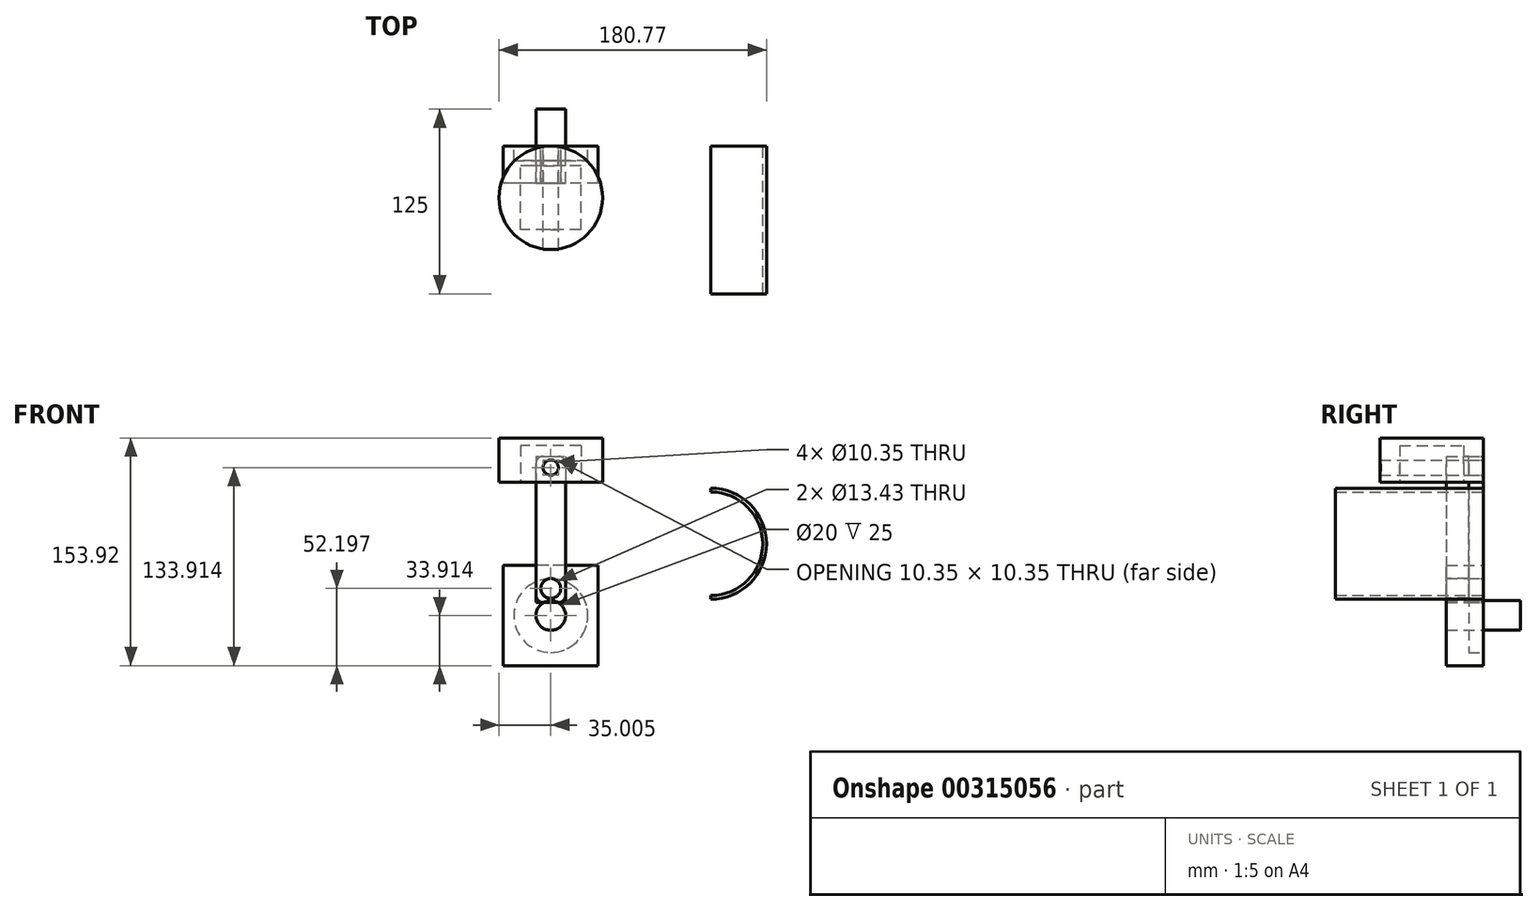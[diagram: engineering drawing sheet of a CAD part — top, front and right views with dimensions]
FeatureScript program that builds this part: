
annotation { "Feature Type Name" : "Feature", "Feature Type Description" : "" }
export const myFeature = defineFeature(function(context is Context, id is Id, definition is map)
    precondition{}
    {
        {
            var Q0;
            Q0=qCreatedBy(makeId("Front.planeOp"),FACE);
            var sketch = newSketch(context, id + "F0", { "sketchPlane" : qUnion([Q0])});
            skCircle(sketch, "E0", {"center": v(-52.9, 10.93) * mm, "radius": 25 * mm});
            skLineSegment(sketch, "E1", {"start": v(-52.9, 19.65) * mm, "end": v(-52.9, 110.93) * mm});
            skLineSegment(sketch, "E2.bottom", {"start": v(-17.9, 100.93) * mm, "end": v(-87.9, 100.93) * mm});
            skLineSegment(sketch, "E2.left", {"start": v(-17.9, 100.93) * mm, "end": v(-17.9, 120.93) * mm});
            skLineSegment(sketch, "E2.right", {"start": v(-87.9, 100.93) * mm, "end": v(-87.9, 120.93) * mm});
            skPoint(sketch, "E2.middle", {"position": v(-52.9, 110.93) * mm});
            skLineSegment(sketch, "E3.left", {"start": v(-62.9, 116.1) * mm, "end": v(-62.9, 19.65) * mm});
            skLineSegment(sketch, "E3.right", {"start": v(-42.9, 116.1) * mm, "end": v(-42.9, 19.65) * mm});
            skPoint(sketch, "E3.middle", {"position": v(-52.9, 60.93) * mm});
            skCircle(sketch, "E4", {"center": v(-52.9, 29.22) * mm, "radius": 6.72 * mm});
            skCircle(sketch, "E5", {"center": v(-52.9, 110.93) * mm, "radius": 5.18 * mm});
            skLineSegment(sketch, "E6.top", {"start": v(-62.9, 118.63) * mm, "end": v(-42.9, 118.63) * mm});
            skLineSegment(sketch, "E6.left", {"start": v(-62.9, 116.1) * mm, "end": v(-62.9, 118.63) * mm});
            skLineSegment(sketch, "E6.right", {"start": v(-42.9, 116.1) * mm, "end": v(-42.9, 118.63) * mm});
            skLineSegment(sketch, "E7.top", {"start": v(-62.9, 19.65) * mm, "end": v(-42.9, 19.65) * mm});
            skPoint(sketch, "E8.orphan", {"position": v(-42.9, 5.76) * mm});
            skPoint(sketch, "E7.bottom.start.orphan", {"position": v(-62.9, 5.76) * mm});
            skLineSegment(sketch, "E9.top", {"start": v(-17.9, 130.94) * mm, "end": v(-87.9, 130.94) * mm});
            skLineSegment(sketch, "E9.left", {"start": v(-17.9, 120.93) * mm, "end": v(-17.9, 130.94) * mm});
            skLineSegment(sketch, "E9.right", {"start": v(-87.9, 120.93) * mm, "end": v(-87.9, 130.94) * mm});
            skCircle(sketch, "E10", {"center": v(-52.9, 10.93) * mm, "radius": 10 * mm});
            skLineSegment(sketch, "E11.bottom", {"start": v(-20.83, 44.84) * mm, "end": v(-84.98, 44.84) * mm});
            skLineSegment(sketch, "E11.top", {"start": v(-20.83, -22.98) * mm, "end": v(-84.98, -22.98) * mm});
            skLineSegment(sketch, "E11.left", {"start": v(-20.83, 44.84) * mm, "end": v(-20.83, -22.98) * mm});
            skLineSegment(sketch, "E11.right", {"start": v(-84.98, 44.84) * mm, "end": v(-84.98, -22.98) * mm});
            skSolve(sketch);
        }
        {
            var Q0;
            Q0=makeQuery(id+"F0.imprint","IMPRINT",FACE,{"disambiguationData":[TD([[makeQuery(id+"F0.imprint","IMPRINT",EDGE,{"derivedFrom":sQuery(id+"F0.wireOp",EDGE,"E2.top")}),1.0]])]});
            var Q1;
            Q1=makeQuery(id+"F0.imprint","IMPRINT",FACE,{"disambiguationData":[TD([[makeQuery(id+"F0.imprint","IMPRINT",EDGE,{"derivedFrom":sQuery(id+"F0.wireOp",EDGE,"E5")}),-1.0]])]});
            var Q2;
            {var subQ7=sQuery(id+"F0.wireOp",EDGE,"E2.left");Q2=makeQuery(id+"F0.imprint","IMPRINT",FACE,{"disambiguationData":[TD([[makeQuery(id+"F0.imprint","IMPRINT",EDGE,{"derivedFrom":subQ7}),1.0]])]});}
            extrude(context, id + "F1", {"entities" : qUnion([Q0, Q1, Q2]), "depth" : 70 * mm});
        }
        {
            var Q0;
            Q0=makeQuery(id+"F1.opExtrude","SWEPT_FACE",FACE,{"disambiguationData":[OSD([sQuery(id+"F0.wireOp",EDGE,"E9.top")])]});
            var sketch = newSketch(context, id + "F2", { "sketchPlane" : qUnion([Q0])});
            skLineSegment(sketch, "E12", {"start": v(-52.9, 0) * mm, "end": v(-52.9, -70) * mm});
            skLineSegment(sketch, "E13", {"start": v(-87.9, -35) * mm, "end": v(-17.9, -35) * mm});
            skCircle(sketch, "E14", {"center": v(-52.9, -35) * mm, "radius": 35 * mm});
            skSolve(sketch);
        }
        {
            var Q0;
            {var subQ1=sQuery(id+"F0.wireOp",EDGE,"E9.top");var subQ2=makeQuery(id+"F1.opExtrude","CAP_EDGE",EDGE,{"disambiguationData":[OSD([subQ1])],"isStart":true});var subQ4=makeQuery(id+"F1.opExtrude","SWEPT_EDGE",EDGE,{"disambiguationData":[OSD([subQ1,sQuery(id+"F0.wireOp",EDGE,"E9.left")])]});var subQ6=makeQuery(id+"F2.imprint","INTERSECT",VERTEX,{"derivedFrom":[subQ4,subQ2]});Q0=makeQuery(id+"F2.imprint","IMPRINT",FACE,{"disambiguationData":[TD([[makeQuery(id+"F2.imprint","IMPRINT",EDGE,{"disambiguationData":[TD([[subQ6,-1.0]])],"derivedFrom":subQ2}),1.0]])]});}
            var Q1;
            {var subQ1=sQuery(id+"F0.wireOp",EDGE,"E9.top");var subQ2=makeQuery(id+"F1.opExtrude","CAP_EDGE",EDGE,{"disambiguationData":[OSD([subQ1])],"isStart":false});var subQ4=makeQuery(id+"F1.opExtrude","SWEPT_EDGE",EDGE,{"disambiguationData":[OSD([subQ1,sQuery(id+"F0.wireOp",EDGE,"E9.right")])]});var subQ6=makeQuery(id+"F2.imprint","INTERSECT",VERTEX,{"derivedFrom":[subQ4,subQ2]});Q1=makeQuery(id+"F2.imprint","IMPRINT",FACE,{"disambiguationData":[TD([[makeQuery(id+"F2.imprint","IMPRINT",EDGE,{"disambiguationData":[TD([[subQ6,1.0]])],"derivedFrom":subQ2}),-1.0]])]});}
            var Q2;
            {var subQ1=sQuery(id+"F0.wireOp",EDGE,"E9.top");var subQ2=makeQuery(id+"F1.opExtrude","CAP_EDGE",EDGE,{"disambiguationData":[OSD([subQ1])],"isStart":false});var subQ4=makeQuery(id+"F1.opExtrude","SWEPT_EDGE",EDGE,{"disambiguationData":[OSD([subQ1,sQuery(id+"F0.wireOp",EDGE,"E9.left")])]});var subQ6=makeQuery(id+"F2.imprint","INTERSECT",VERTEX,{"derivedFrom":[subQ4,subQ2]});Q2=makeQuery(id+"F2.imprint","IMPRINT",FACE,{"disambiguationData":[TD([[makeQuery(id+"F2.imprint","IMPRINT",EDGE,{"disambiguationData":[TD([[subQ6,-1.0]])],"derivedFrom":subQ2}),-1.0]])]});}
            var Q3;
            {var subQ1=sQuery(id+"F0.wireOp",EDGE,"E9.top");var subQ2=makeQuery(id+"F1.opExtrude","CAP_EDGE",EDGE,{"disambiguationData":[OSD([subQ1])],"isStart":true});var subQ4=makeQuery(id+"F1.opExtrude","SWEPT_EDGE",EDGE,{"disambiguationData":[OSD([subQ1,sQuery(id+"F0.wireOp",EDGE,"E9.right")])]});var subQ6=makeQuery(id+"F2.imprint","INTERSECT",VERTEX,{"derivedFrom":[subQ4,subQ2]});Q3=makeQuery(id+"F2.imprint","IMPRINT",FACE,{"disambiguationData":[TD([[makeQuery(id+"F2.imprint","IMPRINT",EDGE,{"disambiguationData":[TD([[subQ6,1.0]])],"derivedFrom":subQ2}),1.0]])]});}
            extrude(context, id + "F3", {"entities" : qUnion([Q0, Q1, Q2, Q3]), "operationType" : NewBodyOperationType.REMOVE, "oppositeDirection" : true, "depth" : 39.5 * mm});
        }
        {
            var Q0;
            Q0=makeQuery(id+"F1.opExtrude","SWEPT_FACE",FACE,{"disambiguationData":[OSD([sQuery(id+"F0.wireOp",EDGE,"E2.bottom")])]});
            var sketch = newSketch(context, id + "F4", { "sketchPlane" : qUnion([Q0])});
            skLineSegment(sketch, "E15", {"start": v(-52.9, 0) * mm, "end": v(-52.9, 70) * mm});
            skLineSegment(sketch, "E16.bottom", {"start": v(-32.5, 56.64) * mm, "end": v(-73.31, 56.64) * mm});
            skLineSegment(sketch, "E16.top", {"start": v(-32.5, 13.36) * mm, "end": v(-73.31, 13.36) * mm});
            skLineSegment(sketch, "E16.left", {"start": v(-32.5, 56.64) * mm, "end": v(-32.5, 13.36) * mm});
            skLineSegment(sketch, "E16.right", {"start": v(-73.31, 56.64) * mm, "end": v(-73.31, 13.36) * mm});
            skPoint(sketch, "E16.middle", {"position": v(-52.9, 35) * mm});
            skSolve(sketch);
        }
        {
            var Q0;
            {var subQ5=sQuery(id+"F4.wireOp",EDGE,"E16.left");Q0=makeQuery(id+"F4.imprint","IMPRINT",FACE,{"disambiguationData":[TD([[makeQuery(id+"F4.imprint","IMPRINT",EDGE,{"derivedFrom":subQ5}),-1.0]])]});}
            var Q1;
            {var subQ5=sQuery(id+"F4.wireOp",EDGE,"E16.right");Q1=makeQuery(id+"F4.imprint","IMPRINT",FACE,{"disambiguationData":[TD([[makeQuery(id+"F4.imprint","IMPRINT",EDGE,{"derivedFrom":subQ5}),1.0]])]});}
            extrude(context, id + "F5", {"entities" : qUnion([Q0, Q1]), "operationType" : NewBodyOperationType.REMOVE, "oppositeDirection" : true, "depth" : 25 * mm});
        }
        {
            var Q0;
            Q0=makeQuery(id+"F0.imprint","IMPRINT",FACE,{"disambiguationData":[TD([[makeQuery(id+"F0.imprint","IMPRINT",EDGE,{"derivedFrom":sQuery(id+"F0.wireOp",EDGE,"E5")}),1.0]])]});
            extrude(context, id + "F6", {"entities" : qUnion([Q0]), "depth" : 70 * mm});
        }
        {
            var Q0;
            {var subQ5=sQuery(id+"F0.wireOp",EDGE,"E0");var subQ7=sQuery(id+"F0.wireOp",EDGE,"E3.right");var subQ9=makeQuery(id+"F0.imprint","INTERSECT",VERTEX,{"derivedFrom":[subQ5,subQ7]});Q0=makeQuery(id+"F0.imprint","IMPRINT",FACE,{"disambiguationData":[TD([[makeQuery(id+"F0.imprint","IMPRINT",EDGE,{"disambiguationData":[TD([[subQ9,1.0]])],"derivedFrom":subQ5}),1.0]])]});}
            var Q1;
            {var subQ0=sQuery(id+"F0.wireOp",EDGE,"E7.top");var subQ1=makeQuery(id+"F0.imprint","INTERSECT",VERTEX,{"derivedFrom":[sQuery(id+"F0.wireOp",EDGE,"E1"),subQ0]});Q1=makeQuery(id+"F0.imprint","IMPRINT",FACE,{"disambiguationData":[TD([[makeQuery(id+"F0.imprint","IMPRINT",EDGE,{"disambiguationData":[TD([[subQ1,1.0]])],"derivedFrom":subQ0}),-1.0]])]});}
            var Q2;
            {var subQ1=sQuery(id+"F0.wireOp",EDGE,"E1");var subQ9=sQuery(id+"F0.wireOp",EDGE,"E10");var subQ11=makeQuery(id+"F0.imprint","INTERSECT",VERTEX,{"derivedFrom":[subQ1,subQ9]});Q2=makeQuery(id+"F0.imprint","IMPRINT",FACE,{"disambiguationData":[TD([[makeQuery(id+"F0.imprint","IMPRINT",EDGE,{"disambiguationData":[TD([[subQ11,-1.0]])],"derivedFrom":subQ1}),1.0]])]});}
            var Q3;
            {var subQ0=sQuery(id+"F0.wireOp",EDGE,"E4");var subQ1=sQuery(id+"F0.wireOp",EDGE,"E1");var subQ2=makeQuery(id+"F0.imprint","INTERSECT",VERTEX,{"derivedFrom":[subQ1,subQ0]});Q3=makeQuery(id+"F0.imprint","IMPRINT",FACE,{"disambiguationData":[TD([[makeQuery(id+"F0.imprint","IMPRINT",EDGE,{"disambiguationData":[TD([[subQ2,-1.0]])],"derivedFrom":subQ1}),1.0]])]});}
            var Q4;
            {var subQ0=sQuery(id+"F0.wireOp",EDGE,"E4");var subQ1=sQuery(id+"F0.wireOp",EDGE,"E1");var subQ2=makeQuery(id+"F0.imprint","INTERSECT",VERTEX,{"derivedFrom":[subQ1,subQ0]});Q4=makeQuery(id+"F0.imprint","IMPRINT",FACE,{"disambiguationData":[TD([[makeQuery(id+"F0.imprint","IMPRINT",EDGE,{"disambiguationData":[TD([[subQ2,-1.0]])],"derivedFrom":subQ1}),-1.0]])]});}
            var Q5;
            {var subQ0=sQuery(id+"F0.wireOp",EDGE,"E7.top");var subQ1=sQuery(id+"F0.wireOp",EDGE,"E1");var subQ2=makeQuery(id+"F0.imprint","INTERSECT",VERTEX,{"derivedFrom":[subQ1,subQ0]});Q5=makeQuery(id+"F0.imprint","IMPRINT",FACE,{"disambiguationData":[TD([[makeQuery(id+"F0.imprint","IMPRINT",EDGE,{"disambiguationData":[TD([[subQ2,-1.0]])],"derivedFrom":subQ1}),-1.0]])]});}
            var Q6;
            {var subQ0=sQuery(id+"F0.wireOp",EDGE,"E7.top");var subQ1=sQuery(id+"F0.wireOp",EDGE,"E1");var subQ2=makeQuery(id+"F0.imprint","INTERSECT",VERTEX,{"derivedFrom":[subQ1,subQ0]});Q6=makeQuery(id+"F0.imprint","IMPRINT",FACE,{"disambiguationData":[TD([[makeQuery(id+"F0.imprint","IMPRINT",EDGE,{"disambiguationData":[TD([[subQ2,-1.0]])],"derivedFrom":subQ1}),1.0]])]});}
            var Q7;
            {var subQ1=sQuery(id+"F0.wireOp",EDGE,"E1");var subQ9=sQuery(id+"F0.wireOp",EDGE,"E10");var subQ10=makeQuery(id+"F0.imprint","INTERSECT",VERTEX,{"derivedFrom":[subQ1,subQ9]});Q7=makeQuery(id+"F0.imprint","IMPRINT",FACE,{"disambiguationData":[TD([[makeQuery(id+"F0.imprint","IMPRINT",EDGE,{"disambiguationData":[TD([[subQ10,-1.0]])],"derivedFrom":subQ1}),-1.0]])]});}
            extrude(context, id + "F7", {"entities" : qUnion([Q0, Q1, Q2, Q3, Q4, Q5, Q6, Q7]), "depth" : 10 * mm});
        }
        {
            var Q0;
            {var subQ0=sQuery(id+"F0.wireOp",EDGE,"E4");var subQ1=sQuery(id+"F0.wireOp",EDGE,"E1");var subQ2=makeQuery(id+"F0.imprint","INTERSECT",VERTEX,{"derivedFrom":[subQ1,subQ0]});Q0=makeQuery(id+"F0.imprint","IMPRINT",FACE,{"disambiguationData":[TD([[makeQuery(id+"F0.imprint","IMPRINT",EDGE,{"disambiguationData":[TD([[subQ2,-1.0]])],"derivedFrom":subQ1}),-1.0]])]});}
            var Q1;
            {var subQ0=sQuery(id+"F0.wireOp",EDGE,"E4");var subQ1=sQuery(id+"F0.wireOp",EDGE,"E1");var subQ2=makeQuery(id+"F0.imprint","INTERSECT",VERTEX,{"derivedFrom":[subQ1,subQ0]});Q1=makeQuery(id+"F0.imprint","IMPRINT",FACE,{"disambiguationData":[TD([[makeQuery(id+"F0.imprint","IMPRINT",EDGE,{"disambiguationData":[TD([[subQ2,-1.0]])],"derivedFrom":subQ1}),1.0]])]});}
            extrude(context, id + "F8", {"entities" : qUnion([Q0, Q1]), "operationType" : NewBodyOperationType.ADD, "depth" : 25 * mm});
        }
        {
            var Q0;
            {var subQ0=sQuery(id+"F0.wireOp",EDGE,"E7.top");var subQ1=makeQuery(id+"F0.imprint","INTERSECT",VERTEX,{"derivedFrom":[sQuery(id+"F0.wireOp",EDGE,"E1"),subQ0]});Q0=makeQuery(id+"F0.imprint","IMPRINT",FACE,{"disambiguationData":[TD([[makeQuery(id+"F0.imprint","IMPRINT",EDGE,{"disambiguationData":[TD([[subQ1,1.0]])],"derivedFrom":subQ0}),-1.0]])]});}
            var Q1;
            {var subQ0=sQuery(id+"F0.wireOp",EDGE,"E7.top");var subQ1=sQuery(id+"F0.wireOp",EDGE,"E1");var subQ2=makeQuery(id+"F0.imprint","INTERSECT",VERTEX,{"derivedFrom":[subQ1,subQ0]});Q1=makeQuery(id+"F0.imprint","IMPRINT",FACE,{"disambiguationData":[TD([[makeQuery(id+"F0.imprint","IMPRINT",EDGE,{"disambiguationData":[TD([[subQ2,-1.0]])],"derivedFrom":subQ1}),1.0]])]});}
            var Q2;
            {var subQ0=sQuery(id+"F0.wireOp",EDGE,"E7.top");var subQ1=sQuery(id+"F0.wireOp",EDGE,"E1");var subQ2=makeQuery(id+"F0.imprint","INTERSECT",VERTEX,{"derivedFrom":[subQ1,subQ0]});Q2=makeQuery(id+"F0.imprint","IMPRINT",FACE,{"disambiguationData":[TD([[makeQuery(id+"F0.imprint","IMPRINT",EDGE,{"disambiguationData":[TD([[subQ2,-1.0]])],"derivedFrom":subQ1}),-1.0]])]});}
            extrude(context, id + "F9", {"entities" : qUnion([Q0, Q1, Q2]), "operationType" : NewBodyOperationType.ADD, "oppositeDirection" : true, "depth" : 25 * mm});
        }
        {
            var Q0;
            Q0=makeQuery(id+"F0.imprint","IMPRINT",FACE,{"disambiguationData":[TD([[makeQuery(id+"F0.imprint","IMPRINT",EDGE,{"derivedFrom":sQuery(id+"F0.wireOp",EDGE,"E11.top")}),-1.0]])]});
            var Q1;
            {var subQ0=sQuery(id+"F0.wireOp",EDGE,"E3.right");var subQ5=sQuery(id+"F0.wireOp",EDGE,"E11.bottom");var subQ6=makeQuery(id+"F0.imprint","INTERSECT",VERTEX,{"derivedFrom":[subQ0,subQ5]});Q1=makeQuery(id+"F0.imprint","IMPRINT",FACE,{"disambiguationData":[TD([[makeQuery(id+"F0.imprint","IMPRINT",EDGE,{"disambiguationData":[TD([[subQ6,-1.0]])],"derivedFrom":subQ0}),-1.0]])]});}
            var Q2;
            {var subQ0=sQuery(id+"F0.wireOp",EDGE,"E3.left");var subQ5=sQuery(id+"F0.wireOp",EDGE,"E11.bottom");var subQ7=makeQuery(id+"F0.imprint","INTERSECT",VERTEX,{"derivedFrom":[subQ0,subQ5]});Q2=makeQuery(id+"F0.imprint","IMPRINT",FACE,{"disambiguationData":[TD([[makeQuery(id+"F0.imprint","IMPRINT",EDGE,{"disambiguationData":[TD([[subQ7,-1.0]])],"derivedFrom":subQ0}),1.0]])]});}
            var Q3;
            {var subQ5=sQuery(id+"F0.wireOp",EDGE,"E0");var subQ7=sQuery(id+"F0.wireOp",EDGE,"E3.right");var subQ9=makeQuery(id+"F0.imprint","INTERSECT",VERTEX,{"derivedFrom":[subQ5,subQ7]});Q3=makeQuery(id+"F0.imprint","IMPRINT",FACE,{"disambiguationData":[TD([[makeQuery(id+"F0.imprint","IMPRINT",EDGE,{"disambiguationData":[TD([[subQ9,1.0]])],"derivedFrom":subQ5}),1.0]])]});}
            var Q4;
            {var subQ1=sQuery(id+"F0.wireOp",EDGE,"E1");var subQ9=sQuery(id+"F0.wireOp",EDGE,"E10");var subQ11=makeQuery(id+"F0.imprint","INTERSECT",VERTEX,{"derivedFrom":[subQ1,subQ9]});Q4=makeQuery(id+"F0.imprint","IMPRINT",FACE,{"disambiguationData":[TD([[makeQuery(id+"F0.imprint","IMPRINT",EDGE,{"disambiguationData":[TD([[subQ11,-1.0]])],"derivedFrom":subQ1}),1.0]])]});}
            var Q5;
            {var subQ1=sQuery(id+"F0.wireOp",EDGE,"E1");var subQ9=sQuery(id+"F0.wireOp",EDGE,"E10");var subQ10=makeQuery(id+"F0.imprint","INTERSECT",VERTEX,{"derivedFrom":[subQ1,subQ9]});Q5=makeQuery(id+"F0.imprint","IMPRINT",FACE,{"disambiguationData":[TD([[makeQuery(id+"F0.imprint","IMPRINT",EDGE,{"disambiguationData":[TD([[subQ10,-1.0]])],"derivedFrom":subQ1}),-1.0]])]});}
            var Q6;
            {var subQ0=sQuery(id+"F0.wireOp",EDGE,"E4");var subQ1=sQuery(id+"F0.wireOp",EDGE,"E1");var subQ2=makeQuery(id+"F0.imprint","INTERSECT",VERTEX,{"derivedFrom":[subQ1,subQ0]});Q6=makeQuery(id+"F0.imprint","IMPRINT",FACE,{"disambiguationData":[TD([[makeQuery(id+"F0.imprint","IMPRINT",EDGE,{"disambiguationData":[TD([[subQ2,-1.0]])],"derivedFrom":subQ1}),-1.0]])]});}
            var Q7;
            {var subQ0=sQuery(id+"F0.wireOp",EDGE,"E4");var subQ1=sQuery(id+"F0.wireOp",EDGE,"E1");var subQ2=makeQuery(id+"F0.imprint","INTERSECT",VERTEX,{"derivedFrom":[subQ1,subQ0]});Q7=makeQuery(id+"F0.imprint","IMPRINT",FACE,{"disambiguationData":[TD([[makeQuery(id+"F0.imprint","IMPRINT",EDGE,{"disambiguationData":[TD([[subQ2,-1.0]])],"derivedFrom":subQ1}),1.0]])]});}
            extrude(context, id + "F10", {"entities" : qUnion([Q0, Q1, Q2, Q3, Q4, Q5, Q6, Q7]), "depth" : 25 * mm});
        }
        {
            var Q0;
            Q0=makeQuery(id+"F0.imprint","IMPRINT",FACE,{"disambiguationData":[TD([[makeQuery(id+"F0.imprint","IMPRINT",EDGE,{"derivedFrom":sQuery(id+"F0.wireOp",EDGE,"E5")}),-1.0]])]});
            var Q1;
            {var subQ0=sQuery(id+"F0.wireOp",EDGE,"E2.bottom");var subQ1=sQuery(id+"F0.wireOp",EDGE,"E1");var subQ2=makeQuery(id+"F0.imprint","INTERSECT",VERTEX,{"derivedFrom":[subQ1,subQ0]});Q1=makeQuery(id+"F0.imprint","IMPRINT",FACE,{"disambiguationData":[TD([[makeQuery(id+"F0.imprint","IMPRINT",EDGE,{"disambiguationData":[TD([[subQ2,1.0]])],"derivedFrom":subQ1}),1.0]])]});}
            var Q2;
            {var subQ0=sQuery(id+"F0.wireOp",EDGE,"E2.bottom");var subQ1=sQuery(id+"F0.wireOp",EDGE,"E1");var subQ2=makeQuery(id+"F0.imprint","INTERSECT",VERTEX,{"derivedFrom":[subQ1,subQ0]});Q2=makeQuery(id+"F0.imprint","IMPRINT",FACE,{"disambiguationData":[TD([[makeQuery(id+"F0.imprint","IMPRINT",EDGE,{"disambiguationData":[TD([[subQ2,1.0]])],"derivedFrom":subQ1}),-1.0]])]});}
            var Q3;
            {var subQ0=sQuery(id+"F0.wireOp",EDGE,"E3.left");var subQ5=sQuery(id+"F0.wireOp",EDGE,"E11.bottom");var subQ7=makeQuery(id+"F0.imprint","INTERSECT",VERTEX,{"derivedFrom":[subQ0,subQ5]});Q3=makeQuery(id+"F0.imprint","IMPRINT",FACE,{"disambiguationData":[TD([[makeQuery(id+"F0.imprint","IMPRINT",EDGE,{"disambiguationData":[TD([[subQ7,-1.0]])],"derivedFrom":subQ0}),1.0]])]});}
            var Q4;
            {var subQ0=sQuery(id+"F0.wireOp",EDGE,"E3.right");var subQ5=sQuery(id+"F0.wireOp",EDGE,"E11.bottom");var subQ6=makeQuery(id+"F0.imprint","INTERSECT",VERTEX,{"derivedFrom":[subQ0,subQ5]});Q4=makeQuery(id+"F0.imprint","IMPRINT",FACE,{"disambiguationData":[TD([[makeQuery(id+"F0.imprint","IMPRINT",EDGE,{"disambiguationData":[TD([[subQ6,-1.0]])],"derivedFrom":subQ0}),-1.0]])]});}
            var Q5;
            {var subQ1=sQuery(id+"F0.wireOp",EDGE,"E1");var subQ9=sQuery(id+"F0.wireOp",EDGE,"E10");var subQ11=makeQuery(id+"F0.imprint","INTERSECT",VERTEX,{"derivedFrom":[subQ1,subQ9]});Q5=makeQuery(id+"F0.imprint","IMPRINT",FACE,{"disambiguationData":[TD([[makeQuery(id+"F0.imprint","IMPRINT",EDGE,{"disambiguationData":[TD([[subQ11,-1.0]])],"derivedFrom":subQ1}),1.0]])]});}
            var Q6;
            {var subQ1=sQuery(id+"F0.wireOp",EDGE,"E1");var subQ9=sQuery(id+"F0.wireOp",EDGE,"E10");var subQ10=makeQuery(id+"F0.imprint","INTERSECT",VERTEX,{"derivedFrom":[subQ1,subQ9]});Q6=makeQuery(id+"F0.imprint","IMPRINT",FACE,{"disambiguationData":[TD([[makeQuery(id+"F0.imprint","IMPRINT",EDGE,{"disambiguationData":[TD([[subQ10,-1.0]])],"derivedFrom":subQ1}),-1.0]])]});}
            var Q7;
            {var subQ0=sQuery(id+"F0.wireOp",EDGE,"E7.top");var subQ1=sQuery(id+"F0.wireOp",EDGE,"E1");var subQ2=makeQuery(id+"F0.imprint","INTERSECT",VERTEX,{"derivedFrom":[subQ1,subQ0]});Q7=makeQuery(id+"F0.imprint","IMPRINT",FACE,{"disambiguationData":[TD([[makeQuery(id+"F0.imprint","IMPRINT",EDGE,{"disambiguationData":[TD([[subQ2,-1.0]])],"derivedFrom":subQ1}),1.0]])]});}
            var Q8;
            {var subQ0=sQuery(id+"F0.wireOp",EDGE,"E7.top");var subQ1=sQuery(id+"F0.wireOp",EDGE,"E1");var subQ2=makeQuery(id+"F0.imprint","INTERSECT",VERTEX,{"derivedFrom":[subQ1,subQ0]});Q8=makeQuery(id+"F0.imprint","IMPRINT",FACE,{"disambiguationData":[TD([[makeQuery(id+"F0.imprint","IMPRINT",EDGE,{"disambiguationData":[TD([[subQ2,-1.0]])],"derivedFrom":subQ1}),-1.0]])]});}
            extrude(context, id + "F11", {"entities" : qUnion([Q0, Q1, Q2, Q3, Q4, Q5, Q6, Q7, Q8]), "depth" : 25 * mm});
        }
        {
            var Q0;
            Q0=makeQuery(id+"F11.opExtrude","SWEPT_EDGE",EDGE,{"disambiguationData":[OSD([sQuery(id+"F0.wireOp",EDGE,"E3.right"),sQuery(id+"F0.wireOp",EDGE,"E7.top")])]});
            var Q1;
            Q1=makeQuery(id+"F11.opExtrude","SWEPT_EDGE",EDGE,{"disambiguationData":[OSD([sQuery(id+"F0.wireOp",EDGE,"E3.left"),sQuery(id+"F0.wireOp",EDGE,"E7.top")])]});
            var Q2;
            Q2=makeQuery(id+"F11.opExtrude","SWEPT_EDGE",EDGE,{"disambiguationData":[OSD([sQuery(id+"F0.wireOp",EDGE,"E6.top"),sQuery(id+"F0.wireOp",EDGE,"E6.left")])]});
            var Q3;
            Q3=makeQuery(id+"F11.opExtrude","SWEPT_EDGE",EDGE,{"disambiguationData":[OSD([sQuery(id+"F0.wireOp",EDGE,"E6.top"),sQuery(id+"F0.wireOp",EDGE,"E6.right")])]});
            fillet(context, id + "F12", {"entities" : qUnion([Q0, Q1, Q2, Q3]), "radius" : 5 * mm, "tangentPropagation" : true, "allowEdgeOverflow" : false});
        }
        {
            var Q0;
            Q0=makeQuery(id+"F11.opExtrude","CAP_FACE",FACE,{"disambiguationData":[OSD([sQuery(id+"F0.wireOp",EDGE,"E3.left"),sQuery(id+"F0.wireOp",EDGE,"E3.right"),sQuery(id+"F0.wireOp",EDGE,"E4"),sQuery(id+"F0.wireOp",EDGE,"E5"),sQuery(id+"F0.wireOp",EDGE,"E6.top"),sQuery(id+"F0.wireOp",EDGE,"E6.left"),sQuery(id+"F0.wireOp",EDGE,"E6.right"),sQuery(id+"F0.wireOp",EDGE,"E7.top")])],"isStart":false});
            extrude(context, id + "F13", {"entities" : qUnion([Q0]), "operationType" : NewBodyOperationType.REMOVE, "oppositeDirection" : true, "depth" : 15 * mm});
        }
        {
            var Q0;
            Q0=qCreatedBy(makeId("Front.planeOp"),FACE);
            var sketch = newSketch(context, id + "F14", { "sketchPlane" : qUnion([Q0])});
            skArc(sketch, "E17", {"start": v(55.36, 24.47) * mm, "mid": v(90.36, 59.47) * mm, "end": v(55.36, 94.47) * mm});
            skArc(sketch, "E18", {"start": v(55.36, 21.97) * mm, "mid": v(92.86, 59.47) * mm, "end": v(55.36, 96.97) * mm});
            skLineSegment(sketch, "E19", {"start": v(55.36, 59.47) * mm, "end": v(55.36, 96.97) * mm});
            skLineSegment(sketch, "E20", {"start": v(55.36, 96.97) * mm, "end": v(55.36, 94.47) * mm});
            skLineSegment(sketch, "E21.trimOffspring", {"start": v(55.36, 24.47) * mm, "end": v(55.36, 21.97) * mm});
            skPoint(sketch, "E22.orphan", {"position": v(55.36, 0) * mm});
            skSolve(sketch);
        }
        {
            var Q0;
            Q0=makeQuery(id+"F14.imprint","IMPRINT",FACE,{"disambiguationData":[TD([[makeQuery(id+"F14.imprint","IMPRINT",EDGE,{"derivedFrom":sQuery(id+"F14.wireOp",EDGE,"E17")}),-1.0]])]});
            extrude(context, id + "F15", {"entities" : qUnion([Q0]), "depth" : 100 * mm});
        }
        {
            var Q0;
            {var subQ0=sQuery(id+"F0.wireOp",EDGE,"E2.bottom");var subQ1=sQuery(id+"F0.wireOp",EDGE,"E1");var subQ2=makeQuery(id+"F0.imprint","INTERSECT",VERTEX,{"derivedFrom":[subQ1,subQ0]});Q0=makeQuery(id+"F0.imprint","IMPRINT",FACE,{"disambiguationData":[TD([[makeQuery(id+"F0.imprint","IMPRINT",EDGE,{"disambiguationData":[TD([[subQ2,1.0]])],"derivedFrom":subQ1}),1.0]])]});}
            var Q1;
            {var subQ0=sQuery(id+"F0.wireOp",EDGE,"E2.bottom");var subQ1=sQuery(id+"F0.wireOp",EDGE,"E1");var subQ2=makeQuery(id+"F0.imprint","INTERSECT",VERTEX,{"derivedFrom":[subQ1,subQ0]});Q1=makeQuery(id+"F0.imprint","IMPRINT",FACE,{"disambiguationData":[TD([[makeQuery(id+"F0.imprint","IMPRINT",EDGE,{"disambiguationData":[TD([[subQ2,1.0]])],"derivedFrom":subQ1}),-1.0]])]});}
            var Q2;
            Q2=makeQuery(id+"F0.imprint","IMPRINT",FACE,{"disambiguationData":[TD([[makeQuery(id+"F0.imprint","IMPRINT",EDGE,{"derivedFrom":sQuery(id+"F0.wireOp",EDGE,"E5")}),-1.0]])]});
            var Q3;
            {var subQ0=sQuery(id+"F0.wireOp",EDGE,"E3.left");var subQ5=sQuery(id+"F0.wireOp",EDGE,"E11.bottom");var subQ7=makeQuery(id+"F0.imprint","INTERSECT",VERTEX,{"derivedFrom":[subQ0,subQ5]});Q3=makeQuery(id+"F0.imprint","IMPRINT",FACE,{"disambiguationData":[TD([[makeQuery(id+"F0.imprint","IMPRINT",EDGE,{"disambiguationData":[TD([[subQ7,-1.0]])],"derivedFrom":subQ0}),1.0]])]});}
            var Q4;
            {var subQ0=sQuery(id+"F0.wireOp",EDGE,"E3.right");var subQ5=sQuery(id+"F0.wireOp",EDGE,"E11.bottom");var subQ6=makeQuery(id+"F0.imprint","INTERSECT",VERTEX,{"derivedFrom":[subQ0,subQ5]});Q4=makeQuery(id+"F0.imprint","IMPRINT",FACE,{"disambiguationData":[TD([[makeQuery(id+"F0.imprint","IMPRINT",EDGE,{"disambiguationData":[TD([[subQ6,-1.0]])],"derivedFrom":subQ0}),-1.0]])]});}
            var Q5;
            {var subQ1=sQuery(id+"F0.wireOp",EDGE,"E1");var subQ9=sQuery(id+"F0.wireOp",EDGE,"E10");var subQ10=makeQuery(id+"F0.imprint","INTERSECT",VERTEX,{"derivedFrom":[subQ1,subQ9]});Q5=makeQuery(id+"F0.imprint","IMPRINT",FACE,{"disambiguationData":[TD([[makeQuery(id+"F0.imprint","IMPRINT",EDGE,{"disambiguationData":[TD([[subQ10,-1.0]])],"derivedFrom":subQ1}),-1.0]])]});}
            var Q6;
            {var subQ1=sQuery(id+"F0.wireOp",EDGE,"E1");var subQ9=sQuery(id+"F0.wireOp",EDGE,"E10");var subQ11=makeQuery(id+"F0.imprint","INTERSECT",VERTEX,{"derivedFrom":[subQ1,subQ9]});Q6=makeQuery(id+"F0.imprint","IMPRINT",FACE,{"disambiguationData":[TD([[makeQuery(id+"F0.imprint","IMPRINT",EDGE,{"disambiguationData":[TD([[subQ11,-1.0]])],"derivedFrom":subQ1}),1.0]])]});}
            var Q7;
            {var subQ0=sQuery(id+"F0.wireOp",EDGE,"E7.top");var subQ1=makeQuery(id+"F0.imprint","INTERSECT",VERTEX,{"derivedFrom":[sQuery(id+"F0.wireOp",EDGE,"E1"),subQ0]});Q7=makeQuery(id+"F0.imprint","IMPRINT",FACE,{"disambiguationData":[TD([[makeQuery(id+"F0.imprint","IMPRINT",EDGE,{"disambiguationData":[TD([[subQ1,1.0]])],"derivedFrom":subQ0}),-1.0]])]});}
            extrude(context, id + "F16", {"entities" : qUnion([Q0, Q1, Q2, Q3, Q4, Q5, Q6, Q7]), "depth" : 25 * mm});
        }
    });
